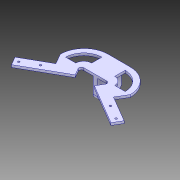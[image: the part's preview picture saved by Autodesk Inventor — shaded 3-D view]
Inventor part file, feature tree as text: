
AUTODESK INVENTOR PART (.ipt)
format: ipt  version: 2018 (Build 220112000, 112)  size: 332,288 bytes
history: native  units: mm
features: extrude x9, sketch x9, other x8, fillet x3
ambient origin geometry x8: Origin, YZ Plane, XZ Plane, XY Plane, X Axis, Y Axis, Z Axis, Center Point
bodies: Body1 (feature_tree)
feature tree (29):
  other  "Sólido1"
  other  "Edición directa1"
  extrude  "Extrusión1"  Depth=30.0mm TaperAngle=0.0deg
  extrude  "Extrusión2"  Depth=48.929mm
  extrude  "Extrusión3"  Depth=20.12mm
  extrude  "Extrusión4"  Depth=2.5mm
  extrude  "Extrusión5"  Depth=2.5mm
  extrude  "Extrusión6"  Depth=5.0mm
  extrude  "Extrusión7"  Depth=6.0mm
  fillet  "Empalme1"  Radius=5.0mm
  fillet  "Empalme2"  Radius=6.0mm
  extrude  "Extrusión8"  Depth=30.0mm TaperAngle=0.0deg
  fillet  "Empalme3"  Radius=30.0mm
  extrude  "Extrusión9"  Depth=30.0mm
  other  "Edición directa2"
  other  "Edición directa3"
  sketch  "Boceto1"  dims[d0=0.0mm d1=0.0mm d2=4.935mm d3=30.0mm d4=0.0mm]
  sketch  "Boceto2"  dims[d5=30.0mm d6=0.0mm d7=48.929mm]
  sketch  "Boceto3"  dims[d8=48.929mm d9=20.12mm]
  sketch  "Boceto4"  dims[d10=20.12mm d11=2.5mm]
  sketch  "Boceto5"  dims[d12=2.5mm d13=2.5mm]
  sketch  "Boceto6"  dims[d14=2.5mm d15=5.0mm]
  sketch  "Boceto7"  dims[d16=6.0mm d17=6.0mm d18=5.0mm d19=6.0mm]
  sketch  "Boceto8"  dims[d20=6.0mm d21=30.0mm d22=0.0mm d23=30.0mm d24=0.0mm]
  sketch  "Boceto9"  dims[d25=30.0mm d26=0.0mm d27=30.0mm d28=30.0mm d29=0.0mm d30=20.0mm d31=5.0mm d32=5.0mm d33=10.0mm d34=30.0mm d35=0.0mm d36=30.0mm d37=3.0mm d40=10.0mm d41=10.0mm d42=22.84mm d43=23.2mm d44=30.0mm d45=0.0mm d46=5.0mm d47=5.0mm d50=30.0deg d60=2.5mm d62=2.5mm d63=4.0mm d64=2.5mm d65=4.0mm d66=10.0mm d67=0.0mm d68=0.0mm d69=0.0mm d70=-2.0mm d71=0.0mm d72=0.0mm d73=-2.0mm]
  other  "PartBody"
  other  "Desplazar1"
  other  "Desplazar2"
  other  "Desplazar3"
